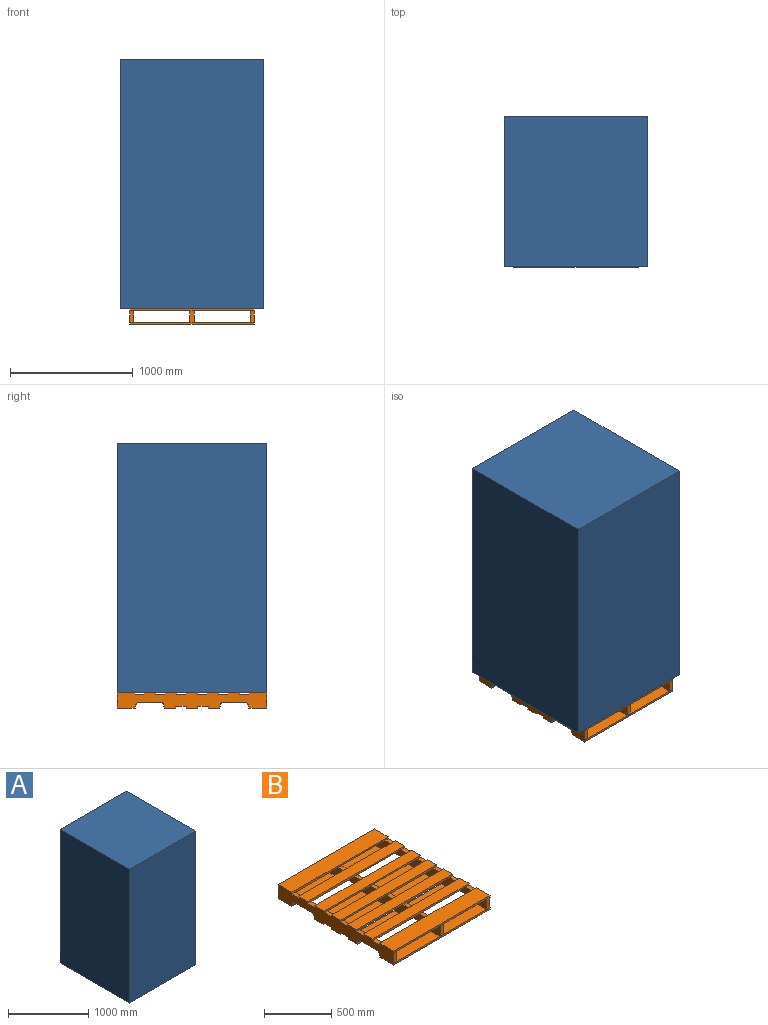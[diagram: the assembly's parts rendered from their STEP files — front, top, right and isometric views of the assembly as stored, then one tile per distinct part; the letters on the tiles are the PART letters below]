
ASSEMBLY  parts=2 mates=1
PART A: 6 faces, bbox 1168.4x1219.2x2032 mm
  f0: plane 2032x1219.2mm, normal (-1,0,0), area 2477414.4mm2, adj f1,f3,f4,f5
  f1: plane 2032x1168.4mm, normal (0,-1,0), area 2374188.8mm2, adj f0,f2,f4,f5
  f2: plane 2032x1219.2mm, normal (1,0,0), area 2477414.4mm2, adj f1,f3,f4,f5
  f3: plane 2032x1168.4mm, normal (0,1,0), area 2374188.8mm2, adj f0,f2,f4,f5
  f4: plane 1219.2x1168.4mm, normal (0,0,1), area 1424513.3mm2, adj f0,f1,f2,f3
  f5: plane 1219.2x1168.4mm, normal (0,0,-1), area 1424513.3mm2, adj f0,f1,f2,f3
PART B: 134 faces, bbox 1016x1219.2x127 mm
  f0: plane 71.8x35mm, normal (0,0,1), area 2513mm2, adj f32,f52,f123,f130
  f1: plane 71.8x35mm, normal (0,0,1), area 2513mm2, adj f68,f69,f123,f130
  f2: plane 71.8x35mm, normal (0,0,1), area 2513mm2, adj f29,f85,f123,f130
  f3: plane 74.8x35mm, normal (0,0,1), area 2618mm2, adj f32,f52,f118,f125
  f4: plane 74.8x35mm, normal (0,0,1), area 2618mm2, adj f68,f69,f118,f125
  f5: plane 74.8x35mm, normal (0,0,1), area 2618mm2, adj f29,f85,f118,f125
  f6: plane 74.8x35mm, normal (0,0,1), area 2618mm2, adj f32,f52,f113,f120
  f7: plane 74.8x35mm, normal (0,0,1), area 2618mm2, adj f68,f69,f113,f120
  f8: plane 74.8x35mm, normal (0,0,1), area 2618mm2, adj f29,f85,f113,f120
  f9: plane 74.8x35mm, normal (0,0,1), area 2618mm2, adj f32,f52,f108,f115
  f10: plane 74.8x35mm, normal (0,0,1), area 2618mm2, adj f68,f69,f108,f115
  f11: plane 74.8x35mm, normal (0,0,1), area 2618mm2, adj f29,f85,f108,f115
  f12: plane 74.8x35mm, normal (0,0,1), area 2618mm2, adj f32,f52,f103,f110
  f13: plane 74.8x35mm, normal (0,0,1), area 2618mm2, adj f32,f52,f105,f126
  f14: plane 74.8x35mm, normal (0,0,1), area 2618mm2, adj f68,f69,f103,f110
  f15: plane 74.8x35mm, normal (0,0,1), area 2618mm2, adj f68,f69,f105,f126
  f16: plane 74.8x35mm, normal (0,0,1), area 2618mm2, adj f29,f85,f103,f110
  f17: plane 74.8x35mm, normal (0,0,1), area 2618mm2, adj f29,f85,f105,f126
  f18: plane 35x0.5mm, normal (0,0,-1), area 17.5mm2, adj f32,f37,f52,f98
  f19: plane 35x0.5mm, normal (0,0,-1), area 17.5mm2, adj f53,f68,f69,f98
  f20: plane 35x0.5mm, normal (0,0,-1), area 17.5mm2, adj f29,f70,f85,f98
  f21: plane 85.2x35mm, normal (0,0,-1), area 2982mm2, adj f32,f52,f93,f100
  f22: plane 85.2x35mm, normal (0,0,-1), area 2982mm2, adj f68,f69,f93,f100
  f23: plane 85.2x35mm, normal (0,0,-1), area 2982mm2, adj f29,f85,f93,f100
  f24: plane 85.2x35mm, normal (0,0,-1), area 2982mm2, adj f32,f52,f88,f95
  f25: plane 85.2x35mm, normal (0,0,-1), area 2982mm2, adj f68,f69,f88,f95
  f26: plane 85.2x35mm, normal (0,0,-1), area 2982mm2, adj f29,f85,f88,f95
  f27: plane 1016x16mm, normal (0,1,0), area 16256mm2, adj f28,f29,f30,f32,f45,f61,f78
  f28: plane 1016x146.2mm, normal (0,0,1), area 133198.7mm2, adj f27,f29,f31,f32,f44,f52,f60,f68
  f29: plane 1219.2x127mm, normal (-1,0,0), area 123447.7mm2, adj f2,f5,f8,f11,f16,f17,f20,f23
  f30: plane 1016x146.2mm, normal (0,0,-1), area 148539.2mm2, adj f27,f29,f31,f32
  f31: plane 1016x16mm, normal (0,-1,0), area 16256mm2, adj f28,f29,f30,f32
  f32: plane 1219.2x127mm, normal (1,0,0), area 123447.7mm2, adj f0,f3,f6,f9,f12,f13,f18,f21
  f33: plane 1016x16mm, normal (0,1,0), area 16256mm2, adj f29,f32,f34,f35
  f34: plane 1016x146.2mm, normal (0,0,1), area 133198.7mm2, adj f29,f32,f33,f36,f43,f52,f59,f68
  f35: plane 1016x146.2mm, normal (0,0,-1), area 148539.2mm2, adj f29,f32,f33,f36
  f36: plane 1016x16mm, normal (0,-1,0), area 16256mm2, adj f29,f32,f34,f35,f42,f58,f75
  f37: plane 35x12.2mm, normal (0,1,0), area 427mm2, adj f18,f32,f38,f52
  f38: cylinder r=19mm len=35mm, axis (-1,0,0), area 1044.6mm2, adj f32,f37,f39,f52
  f39: plane 191x35mm, normal (0,0,-1), area 6685mm2, adj f32,f38,f40,f52
  f40: cylinder r=19mm len=35mm, axis (-1,0,0), area 1044.6mm2, adj f32,f39,f41,f52
  f41: plane 35x12.2mm, normal (0,-1,0), area 427mm2, adj f32,f40,f42,f52
  f42: plane 35x5.9mm, normal (0,0,-1), area 206.5mm2, adj f32,f36,f41,f52
  f43: plane 95x35mm, normal (0,1,0), area 3325mm2, adj f32,f34,f52,f132
  f44: plane 95x35mm, normal (0,-1,0), area 3325mm2, adj f28,f32,f52,f128
  f45: plane 35x5.9mm, normal (0,0,-1), area 206.5mm2, adj f27,f32,f46,f52
  f46: plane 35x12.2mm, normal (0,1,0), area 427mm2, adj f32,f45,f47,f52
  f47: cylinder r=19mm len=35mm, axis (-1,0,0), area 1044.6mm2, adj f32,f46,f48,f52
  f48: plane 191x35mm, normal (0,0,-1), area 6685mm2, adj f32,f47,f49,f52
  f49: cylinder r=19mm len=35mm, axis (-1,0,0), area 1044.6mm2, adj f32,f48,f50,f52
  f50: plane 35x12.2mm, normal (0,-1,0), area 427mm2, adj f32,f49,f51,f52
  f51: plane 35x0.5mm, normal (0,0,-1), area 17.5mm2, adj f32,f50,f52,f90
  f52: plane 1219x95mm, normal (-1,0,0), area 101825.3mm2, adj f0,f3,f6,f9,f12,f13,f18,f21
  f53: plane 35x12.2mm, normal (0,1,0), area 427mm2, adj f19,f54,f68,f69
  f54: cylinder r=19mm len=35mm, axis (-1,0,0), area 1044.6mm2, adj f53,f55,f68,f69
  f55: plane 191x35mm, normal (0,0,-1), area 6685mm2, adj f54,f56,f68,f69
  f56: cylinder r=19mm len=35mm, axis (-1,0,0), area 1044.6mm2, adj f55,f57,f68,f69
  f57: plane 35x12.2mm, normal (0,-1,0), area 427mm2, adj f56,f58,f68,f69
  f58: plane 35x5.9mm, normal (0,0,-1), area 206.5mm2, adj f36,f57,f68,f69
  f59: plane 95x35mm, normal (0,1,0), area 3325mm2, adj f34,f68,f69,f132
  f60: plane 95x35mm, normal (0,-1,0), area 3325mm2, adj f28,f68,f69,f128
  f61: plane 35x5.9mm, normal (0,0,-1), area 206.5mm2, adj f27,f62,f68,f69
  f62: plane 35x12.2mm, normal (0,1,0), area 427mm2, adj f61,f63,f68,f69
  f63: cylinder r=19mm len=35mm, axis (-1,0,0), area 1044.6mm2, adj f62,f64,f68,f69
  f64: plane 191x35mm, normal (0,0,-1), area 6685mm2, adj f63,f65,f68,f69
  f65: cylinder r=19mm len=35mm, axis (-1,0,0), area 1044.6mm2, adj f64,f66,f68,f69
  f66: plane 35x12.2mm, normal (0,-1,0), area 427mm2, adj f65,f67,f68,f69
  f67: plane 35x0.5mm, normal (0,0,-1), area 17.5mm2, adj f66,f68,f69,f90
  f68: plane 1219x95mm, normal (1,0,0), area 101825.3mm2, adj f1,f4,f7,f10,f14,f15,f19,f22
  f69: plane 1219x95mm, normal (-1,0,0), area 101825.3mm2, adj f1,f4,f7,f10,f14,f15,f19,f22
  f70: plane 35x12.2mm, normal (0,1,0), area 427mm2, adj f20,f29,f71,f85
  f71: cylinder r=19mm len=35mm, axis (-1,0,0), area 1044.6mm2, adj f29,f70,f72,f85
  f72: plane 191x35mm, normal (0,0,-1), area 6685mm2, adj f29,f71,f73,f85
  f73: cylinder r=19mm len=35mm, axis (-1,0,0), area 1044.6mm2, adj f29,f72,f74,f85
  f74: plane 35x12.2mm, normal (0,-1,0), area 427mm2, adj f29,f73,f75,f85
  f75: plane 35x5.9mm, normal (0,0,-1), area 206.5mm2, adj f29,f36,f74,f85
  f76: plane 95x35mm, normal (0,1,0), area 3325mm2, adj f29,f34,f85,f132
  f77: plane 95x35mm, normal (0,-1,0), area 3325mm2, adj f28,f29,f85,f128
  f78: plane 35x5.9mm, normal (0,0,-1), area 206.5mm2, adj f27,f29,f79,f85
  f79: plane 35x12.2mm, normal (0,1,0), area 427mm2, adj f29,f78,f80,f85
  f80: cylinder r=19mm len=35mm, axis (-1,0,0), area 1044.6mm2, adj f29,f79,f81,f85
  f81: plane 191x35mm, normal (0,0,-1), area 6685mm2, adj f29,f80,f82,f85
  f82: cylinder r=19mm len=35mm, axis (-1,0,0), area 1044.6mm2, adj f29,f81,f83,f85
  f83: plane 35x12.2mm, normal (0,-1,0), area 427mm2, adj f29,f82,f84,f85
  f84: plane 35x0.5mm, normal (0,0,-1), area 17.5mm2, adj f29,f83,f85,f90
  f85: plane 1219x95mm, normal (1,0,0), area 101825.3mm2, adj f2,f5,f8,f11,f16,f17,f20,f23
  f86: plane 455.5x95.2mm, normal (0,0,1), area 43363.6mm2, adj f52,f68,f88,f90
  f87: plane 455.5x95.2mm, normal (0,0,1), area 43363.6mm2, adj f69,f85,f88,f90
  f88: plane 1016x16mm, normal (0,1,0), area 16256mm2, adj f24,f25,f26,f29,f32,f86,f87,f89
  f89: plane 1016x95.2mm, normal (0,0,-1), area 96723.2mm2, adj f29,f32,f88,f90
  f90: plane 1016x16mm, normal (0,-1,0), area 16256mm2, adj f29,f32,f51,f67,f84,f86,f87,f89
  f91: plane 455.5x95.2mm, normal (0,0,1), area 43363.6mm2, adj f52,f68,f93,f95
  f92: plane 455.5x95.2mm, normal (0,0,1), area 43363.6mm2, adj f69,f85,f93,f95
  f93: plane 1016x16mm, normal (0,1,0), area 16256mm2, adj f21,f22,f23,f29,f32,f91,f92,f94
  f94: plane 1016x95.2mm, normal (0,0,-1), area 96723.2mm2, adj f29,f32,f93,f95
  f95: plane 1016x16mm, normal (0,-1,0), area 16256mm2, adj f24,f25,f26,f29,f32,f91,f92,f94
  f96: plane 455.5x95.2mm, normal (0,0,1), area 43363.6mm2, adj f52,f68,f98,f100
  f97: plane 455.5x95.2mm, normal (0,0,1), area 43363.6mm2, adj f69,f85,f98,f100
  f98: plane 1016x16mm, normal (0,1,0), area 16256mm2, adj f18,f19,f20,f29,f32,f96,f97,f99
  f99: plane 1016x95.2mm, normal (0,0,-1), area 96723.2mm2, adj f29,f32,f98,f100
  f100: plane 1016x16mm, normal (0,-1,0), area 16256mm2, adj f21,f22,f23,f29,f32,f96,f97,f99
  f101: plane 455.5x96.2mm, normal (0,0,-1), area 43819.1mm2, adj f52,f68,f103,f105
  f102: plane 455.5x96.2mm, normal (0,0,-1), area 43819.1mm2, adj f69,f85,f103,f105
  f103: plane 1016x16mm, normal (0,1,0), area 16256mm2, adj f12,f14,f16,f29,f32,f101,f102,f104
  f104: plane 1016x96.2mm, normal (0,0,1), area 97739.2mm2, adj f29,f32,f103,f105
  f105: plane 1016x16mm, normal (0,-1,0), area 16256mm2, adj f13,f15,f17,f29,f32,f101,f102,f104
  f106: plane 455.5x96.2mm, normal (0,0,-1), area 43819.1mm2, adj f52,f68,f108,f110
  f107: plane 455.5x96.2mm, normal (0,0,-1), area 43819.1mm2, adj f69,f85,f108,f110
  f108: plane 1016x16mm, normal (0,1,0), area 16256mm2, adj f9,f10,f11,f29,f32,f106,f107,f109
  f109: plane 1016x96.2mm, normal (0,0,1), area 97739.2mm2, adj f29,f32,f108,f110
  f110: plane 1016x16mm, normal (0,-1,0), area 16256mm2, adj f12,f14,f16,f29,f32,f106,f107,f109
  f111: plane 455.5x96.2mm, normal (0,0,-1), area 43819.1mm2, adj f52,f68,f113,f115
  f112: plane 455.5x96.2mm, normal (0,0,-1), area 43819.1mm2, adj f69,f85,f113,f115
  f113: plane 1016x16mm, normal (0,1,0), area 16256mm2, adj f6,f7,f8,f29,f32,f111,f112,f114
  f114: plane 1016x96.2mm, normal (0,0,1), area 97739.2mm2, adj f29,f32,f113,f115
  f115: plane 1016x16mm, normal (0,-1,0), area 16256mm2, adj f9,f10,f11,f29,f32,f111,f112,f114
  f116: plane 455.5x96.2mm, normal (0,0,-1), area 43819.1mm2, adj f52,f68,f118,f120
  f117: plane 455.5x96.2mm, normal (0,0,-1), area 43819.1mm2, adj f69,f85,f118,f120
  f118: plane 1016x16mm, normal (0,1,0), area 16256mm2, adj f3,f4,f5,f29,f32,f116,f117,f119
  f119: plane 1016x96.2mm, normal (0,0,1), area 97739.2mm2, adj f29,f32,f118,f120
  f120: plane 1016x16mm, normal (0,-1,0), area 16256mm2, adj f6,f7,f8,f29,f32,f116,f117,f119
  f121: plane 455.5x96.2mm, normal (0,0,-1), area 43819.1mm2, adj f52,f68,f123,f125
  f122: plane 455.5x96.2mm, normal (0,0,-1), area 43819.1mm2, adj f69,f85,f123,f125
  f123: plane 1016x16mm, normal (0,1,0), area 16256mm2, adj f0,f1,f2,f29,f32,f121,f122,f124
  f124: plane 1016x96.2mm, normal (0,0,1), area 97739.2mm2, adj f29,f32,f123,f125
  f125: plane 1016x16mm, normal (0,-1,0), area 16256mm2, adj f3,f4,f5,f29,f32,f121,f122,f124
  f126: plane 1016x16mm, normal (0,1,0), area 16256mm2, adj f13,f15,f17,f29,f32,f127,f128
  f127: plane 1016x146.2mm, normal (0,0,1), area 148539.2mm2, adj f29,f32,f126,f129
  f128: plane 1016x146.2mm, normal (0,0,-1), area 133198.7mm2, adj f29,f32,f44,f52,f60,f68,f69,f77
  f129: plane 1016x16mm, normal (0,-1,0), area 16256mm2, adj f29,f32,f127,f128
  f130: plane 1016x16mm, normal (0,-1,0), area 16256mm2, adj f0,f1,f2,f29,f32,f131,f132
  f131: plane 1016x146.2mm, normal (0,0,1), area 148539.2mm2, adj f29,f32,f130,f133
  f132: plane 1016x146.2mm, normal (0,0,-1), area 133198.7mm2, adj f29,f32,f43,f52,f59,f68,f69,f76
  f133: plane 1016x16mm, normal (0,1,0), area 16256mm2, adj f29,f32,f131,f132
PLACE A t=(1144.9,39.3,148.31)mm
PLACE B t=(1729.1,648.9,21.31)mm
MATE fastened B.f129 <-> A.f1  axis (0,-1,0) through (1729.1,39.3,148.31)mm
